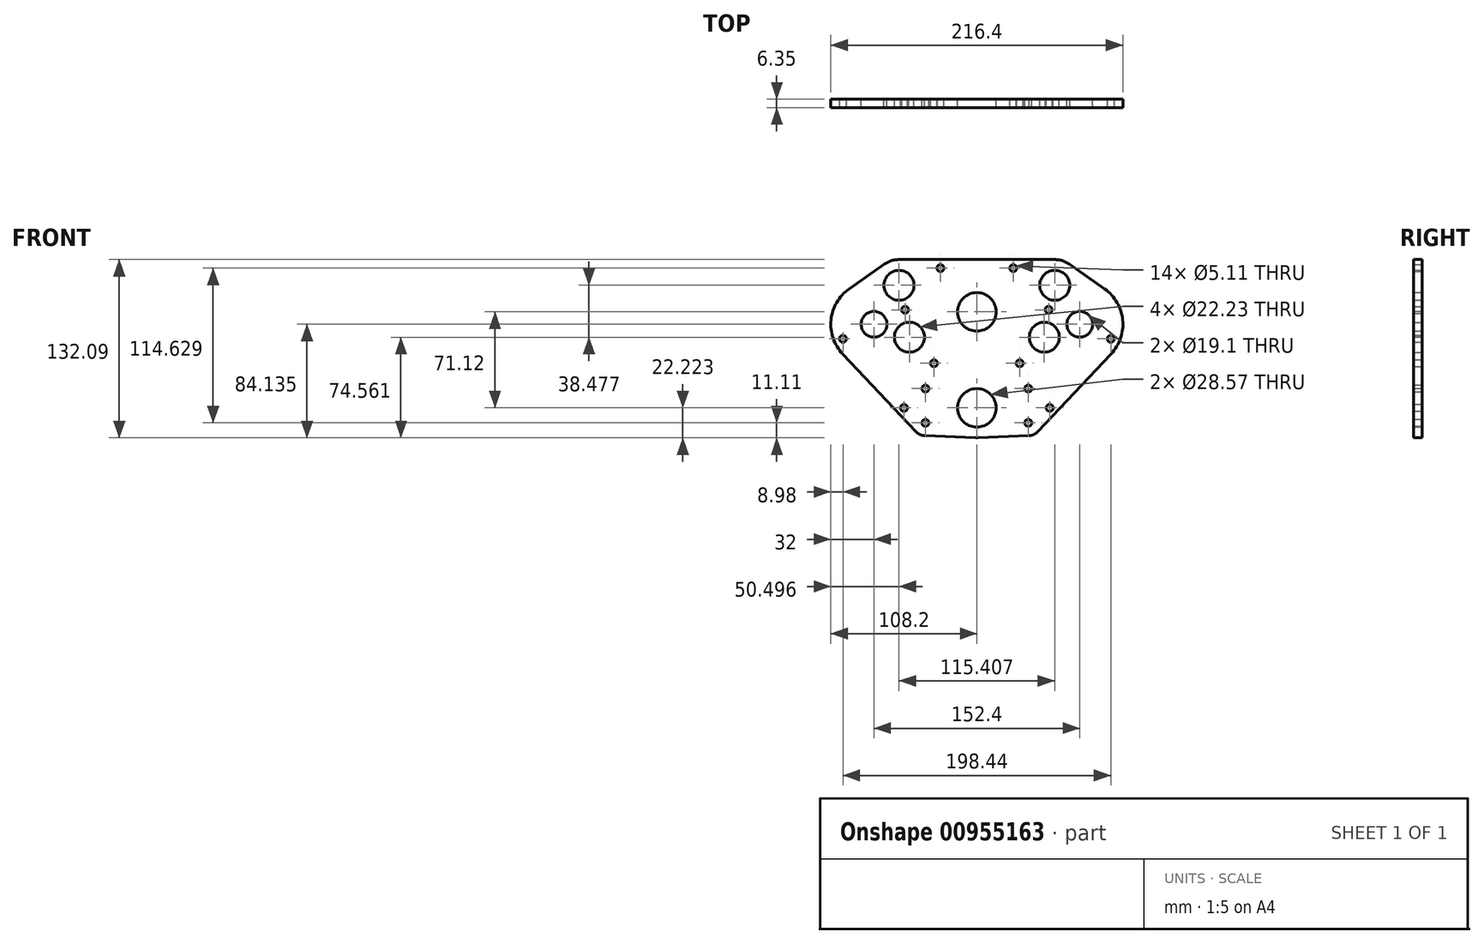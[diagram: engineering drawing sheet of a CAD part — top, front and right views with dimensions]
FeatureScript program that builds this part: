
annotation { "Feature Type Name" : "Feature", "Feature Type Description" : "" }
export const myFeature = defineFeature(function(context is Context, id is Id, definition is map)
    precondition{}
    {
        {
            var Q0;
            Q0=qCreatedBy(makeId("Front.planeOp"),FACE);
            var sketch = newSketch(context, id + "F0", { "sketchPlane" : qUnion([Q0])});
            skCircle(sketch, "E0", {"center": v(-76.2, 60.32) * mm, "radius": 32 * mm, "construction": true});
            skCircle(sketch, "E1", {"center": v(76.2, 60.33) * mm, "radius": 32 * mm, "construction": true});
            skLineSegment(sketch, "E2", {"start": v(-76.2, 60.32) * mm, "end": v(76.2, 60.32) * mm, "construction": true});
            skLineSegment(sketch, "E3", {"start": v(0, 60.32) * mm, "end": v(0, 0) * mm, "construction": true});
            skCircle(sketch, "E4", {"center": v(-76.2, 60.32) * mm, "radius": 7.63 * mm, "construction": true});
            skCircle(sketch, "E5", {"center": v(76.2, 60.33) * mm, "radius": 7.63 * mm, "construction": true});
            skLineSegment(sketch, "E6.bottom", {"start": v(-127, 25.4) * mm, "end": v(127, 25.4) * mm, "construction": true});
            skLineSegment(sketch, "E6.top", {"start": v(-127, -25.4) * mm, "end": v(127, -25.4) * mm, "construction": true});
            skLineSegment(sketch, "E6.left", {"start": v(-127, 25.4) * mm, "end": v(-127, -25.4) * mm, "construction": true});
            skLineSegment(sketch, "E6.right", {"start": v(127, 25.4) * mm, "end": v(127, -25.4) * mm, "construction": true});
            skPoint(sketch, "E6.middle", {"position": v(0, -1.59) * mm});
            skCircle(sketch, "E7", {"center": v(0, -1.59) * mm, "radius": 50.8 * mm, "construction": true});
            skCircle(sketch, "E8", {"center": v(-57.7, 89.23) * mm, "radius": 26.68 * mm, "construction": true});
            skCircle(sketch, "E9", {"center": v(57.7, 89.23) * mm, "radius": 26.68 * mm, "construction": true});
            skCircle(sketch, "E10", {"center": v(0, 69.53) * mm, "radius": 34.3 * mm, "construction": true});
            skCircle(sketch, "E11", {"center": v(0, 69.53) * mm, "radius": 25.4 * mm, "construction": true});
            skCircle(sketch, "E12", {"center": v(0, 69.53) * mm, "radius": 38.1 * mm, "construction": true});
            skCircle(sketch, "E13", {"center": v(0, -1.59) * mm, "radius": 33.02 * mm, "construction": true});
            skCircle(sketch, "E14", {"center": v(0, -1.59) * mm, "radius": 45.72 * mm, "construction": true});
            skCircle(sketch, "E15", {"center": v(-76.2, 60.32) * mm, "radius": 9.55 * mm});
            skCircle(sketch, "E16", {"center": v(76.2, 60.33) * mm, "radius": 9.55 * mm});
            skCircle(sketch, "E17", {"center": v(-57.7, 89.23) * mm, "radius": 11.11 * mm});
            skCircle(sketch, "E18", {"center": v(57.7, 89.23) * mm, "radius": 11.11 * mm});
            skCircle(sketch, "E19", {"center": v(0, 69.53) * mm, "radius": 14.29 * mm});
            skCircle(sketch, "E20", {"center": v(0, -1.59) * mm, "radius": 14.29 * mm});
            skPoint(sketch, "E21.middle", {"position": v(0, 0) * mm});
            skCircle(sketch, "E22", {"center": v(-38.1, 12.7) * mm, "radius": 9.53 * mm, "construction": true});
            skCircle(sketch, "E23", {"center": v(-38.1, -12.7) * mm, "radius": 9.53 * mm, "construction": true});
            skCircle(sketch, "E24", {"center": v(38.1, -12.7) * mm, "radius": 9.53 * mm, "construction": true});
            skCircle(sketch, "E25", {"center": v(38.1, 12.7) * mm, "radius": 9.53 * mm, "construction": true});
            skCircle(sketch, "E26", {"center": v(38.1, 0) * mm, "radius": 9.53 * mm, "construction": true});
            skCircle(sketch, "E27", {"center": v(-38.1, 0) * mm, "radius": 9.53 * mm, "construction": true});
            skCircle(sketch, "E28", {"center": v(38.1, -12.7) * mm, "radius": 2.55 * mm});
            skCircle(sketch, "E29", {"center": v(38.1, 0) * mm, "radius": 2.55 * mm, "construction": true});
            skCircle(sketch, "E30", {"center": v(38.1, 12.7) * mm, "radius": 2.55 * mm});
            skCircle(sketch, "E31", {"center": v(-38.1, 12.7) * mm, "radius": 2.55 * mm});
            skCircle(sketch, "E32", {"center": v(-38.1, 0) * mm, "radius": 2.55 * mm, "construction": true});
            skCircle(sketch, "E33", {"center": v(-38.1, -12.7) * mm, "radius": 2.55 * mm});
            skLineSegment(sketch, "E34", {"start": v(-45.02, -19.24) * mm, "end": v(-99.46, 38.34) * mm});
            skArc(sketch, "E35", {"start": v(-45.02, -19.24) * mm, "mid": v(-42.05, -21.37) * mm, "end": v(-38.5, -22.22) * mm});
            skArc(sketch, "E36", {"start": v(38.5, -22.22) * mm, "mid": v(42.05, -21.37) * mm, "end": v(45.02, -19.24) * mm});
            skLineSegment(sketch, "E37", {"start": v(45.02, -19.24) * mm, "end": v(99.46, 38.34) * mm});
            skCircle(sketch, "E38", {"center": v(57.7, 89.23) * mm, "radius": 19.05 * mm, "construction": true});
            skCircle(sketch, "E39", {"center": v(-57.7, 89.23) * mm, "radius": 19.05 * mm, "construction": true});
            skArc(sketch, "E40", {"start": v(99.46, 38.34) * mm, "mid": v(108.05, 63.5) * mm, "end": v(94.65, 86.48) * mm});
            skArc(sketch, "E41", {"start": v(-94.65, 86.48) * mm, "mid": v(-108.05, 63.5) * mm, "end": v(-99.46, 38.34) * mm});
            skLineSegment(sketch, "E42", {"start": v(-53.18, 71.06) * mm, "end": v(-76.2, 60.32) * mm, "construction": true});
            skLineSegment(sketch, "E43", {"start": v(-76.2, 60.32) * mm, "end": v(-99.22, 49.6) * mm, "construction": true});
            skCircle(sketch, "E44", {"center": v(-99.22, 49.6) * mm, "radius": 2.55 * mm});
            skCircle(sketch, "E45", {"center": v(-53.18, 71.06) * mm, "radius": 2.55 * mm});
            skCircle(sketch, "E46.MirrorC", {"center": v(53.18, 71.06) * mm, "radius": 2.55 * mm});
            skLineSegment(sketch, "E47.MirrorCS", {"start": v(53.18, 71.06) * mm, "end": v(76.2, 60.33) * mm, "construction": true});
            skLineSegment(sketch, "E48.MirrorCS", {"start": v(76.2, 60.33) * mm, "end": v(99.22, 49.6) * mm, "construction": true});
            skCircle(sketch, "E49.MirrorC", {"center": v(99.22, 49.6) * mm, "radius": 2.55 * mm});
            skLineSegment(sketch, "E50", {"start": v(94.65, 86.48) * mm, "end": v(68.69, 104.8) * mm});
            skLineSegment(sketch, "E51", {"start": v(-94.65, 86.48) * mm, "end": v(-68.69, 104.8) * mm});
            skLineSegment(sketch, "E52", {"start": v(-57.7, 108.28) * mm, "end": v(57.7, 108.28) * mm});
            skArc(sketch, "E53", {"start": v(-68.69, 104.8) * mm, "mid": v(-63.46, 107.39) * mm, "end": v(-57.7, 108.28) * mm});
            skArc(sketch, "E54", {"start": v(57.7, 108.28) * mm, "mid": v(63.46, 107.39) * mm, "end": v(68.69, 104.8) * mm});
            skCircle(sketch, "E55", {"center": v(0, -1.59) * mm, "radius": 22.23 * mm, "construction": true});
            skLineSegment(sketch, "E56", {"start": v(38.5, -22.22) * mm, "end": v(0.93, -23.8) * mm});
            skLineSegment(sketch, "E57", {"start": v(-38.5, -22.22) * mm, "end": v(-0.93, -23.8) * mm});
            skArc(sketch, "E58", {"start": v(-0.93, -23.8) * mm, "mid": v(0, -23.81) * mm, "end": v(0.93, -23.8) * mm});
            skLineSegment(sketch, "E59.bottom", {"start": v(-38.1, -12.7) * mm, "end": v(38.1, -12.7) * mm, "construction": true});
            skLineSegment(sketch, "E59.top", {"start": v(-38.1, 12.7) * mm, "end": v(38.1, 12.7) * mm, "construction": true});
            skLineSegment(sketch, "E59.left", {"start": v(-38.1, -12.7) * mm, "end": v(-38.1, 12.7) * mm, "construction": true});
            skLineSegment(sketch, "E59.right", {"start": v(38.1, -12.7) * mm, "end": v(38.1, 12.7) * mm, "construction": true});
            skCircle(sketch, "E60", {"center": v(-26.99, 101.93) * mm, "radius": 6.35 * mm, "construction": true});
            skCircle(sketch, "E61", {"center": v(-26.99, 101.93) * mm, "radius": 2.55 * mm});
            skCircle(sketch, "E62.MirrorC", {"center": v(26.99, 101.93) * mm, "radius": 6.35 * mm, "construction": true});
            skCircle(sketch, "E63.MirrorC", {"center": v(26.99, 101.93) * mm, "radius": 2.55 * mm});
            skCircle(sketch, "E64", {"center": v(-53.97, -1.59) * mm, "radius": 7.94 * mm, "construction": true});
            skCircle(sketch, "E65", {"center": v(-53.97, -1.59) * mm, "radius": 2.55 * mm});
            skCircle(sketch, "E66.MirrorC", {"center": v(53.98, -1.59) * mm, "radius": 7.94 * mm, "construction": true});
            skCircle(sketch, "E67.MirrorC", {"center": v(53.98, -1.59) * mm, "radius": 2.55 * mm});
            skCircle(sketch, "E68", {"center": v(-31.75, 31.43) * mm, "radius": 6.35 * mm, "construction": true});
            skCircle(sketch, "E69", {"center": v(31.75, 31.43) * mm, "radius": 6.35 * mm, "construction": true});
            skCircle(sketch, "E70", {"center": v(31.75, 31.43) * mm, "radius": 2.55 * mm});
            skCircle(sketch, "E71", {"center": v(-31.75, 31.43) * mm, "radius": 2.55 * mm});
            skLineSegment(sketch, "E72", {"start": v(31.75, 31.43) * mm, "end": v(-31.75, 31.43) * mm, "construction": true});
            skLineSegment(sketch, "E73", {"start": v(0, 31.43) * mm, "end": v(0, 69.53) * mm, "construction": true});
            skCircle(sketch, "E74", {"center": v(-76.2, 60.32) * mm, "radius": 8.9 * mm, "construction": true});
            skCircle(sketch, "E75", {"center": v(76.2, 60.33) * mm, "radius": 8.9 * mm, "construction": true});
            skCircle(sketch, "E76", {"center": v(-49.94, 50.75) * mm, "radius": 19.06 * mm, "construction": true});
            skCircle(sketch, "E77", {"center": v(-49.94, 50.75) * mm, "radius": 11.11 * mm});
            skCircle(sketch, "E78.MirrorC", {"center": v(49.94, 50.75) * mm, "radius": 11.11 * mm});
            skCircle(sketch, "E79.MirrorC", {"center": v(49.94, 50.75) * mm, "radius": 19.06 * mm, "construction": true});
            skLineSegment(sketch, "E80", {"start": v(0, 12.7) * mm, "end": v(0, -1.59) * mm, "construction": true});
            skLineSegment(sketch, "E81", {"start": v(-14.29, -1.59) * mm, "end": v(14.29, -1.59) * mm, "construction": true});
            skLineSegment(sketch, "E82", {"start": v(0, 0) * mm, "end": v(0, 25.4) * mm, "construction": true});
            skSolve(sketch);
        }
        {
            var Q0;
            Q0=qSketchRegion(id+"F0",true);
            extrude(context, id + "F1", {"entities" : qUnion([Q0]), "depth" : 6.35 * mm, "offsetDistance" : 25.4 * mm});
        }
    });
